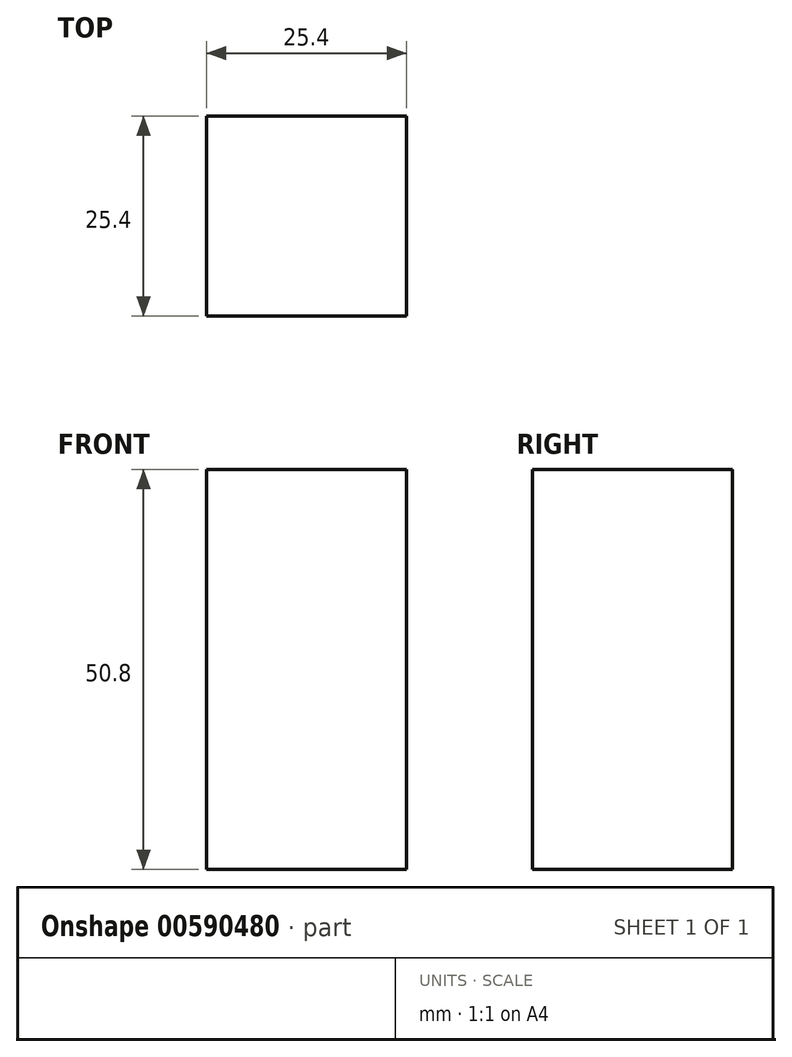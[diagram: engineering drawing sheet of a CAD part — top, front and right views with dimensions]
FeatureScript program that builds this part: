
annotation { "Feature Type Name" : "Feature", "Feature Type Description" : "" }
export const myFeature = defineFeature(function(context is Context, id is Id, definition is map)
    precondition{}
    {
        {
            var Q0;
            Q0=qCreatedBy(makeId("Top.planeOp"),FACE);
            var sketch = newSketch(context, id + "F0", { "sketchPlane" : qUnion([Q0])});
            skLineSegment(sketch, "E0.bottom", {"start": v(12.7, -12.7) * mm, "end": v(-12.7, -12.7) * mm});
            skLineSegment(sketch, "E0.top", {"start": v(12.7, 12.7) * mm, "end": v(-12.7, 12.7) * mm});
            skLineSegment(sketch, "E0.left", {"start": v(12.7, -12.7) * mm, "end": v(12.7, 12.7) * mm});
            skLineSegment(sketch, "E0.right", {"start": v(-12.7, -12.7) * mm, "end": v(-12.7, 12.7) * mm});
            skPoint(sketch, "E0.middle", {"position": v(0, 0) * mm});
            skSolve(sketch);
        }
        {
            var Q0;
            Q0=makeQuery(id+"F0.imprint","IMPRINT",FACE,{"disambiguationData":[TD([[makeQuery(id+"F0.imprint","IMPRINT",EDGE,{"derivedFrom":sQuery(id+"F0.wireOp",EDGE,"E0.bottom")}),-1.0]])]});
            extrude(context, id + "F1", {"entities" : qUnion([Q0]), "depth" : 50.8 * mm, "offsetDistance" : 25.4 * mm});
        }
    });
